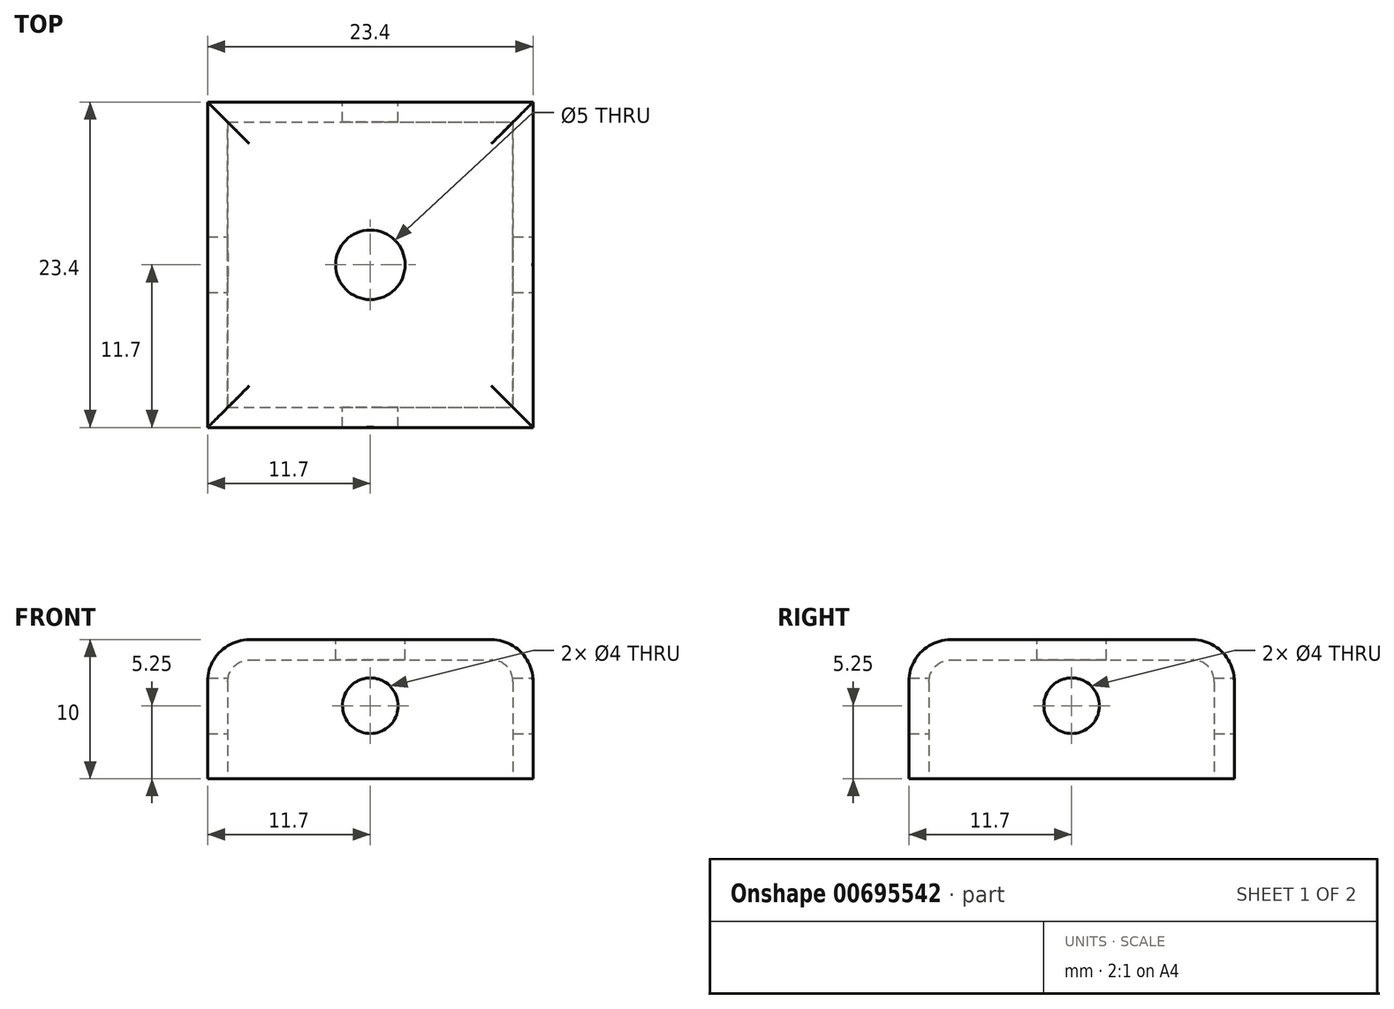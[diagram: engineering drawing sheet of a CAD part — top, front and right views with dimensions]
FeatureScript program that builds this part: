
annotation { "Feature Type Name" : "Feature", "Feature Type Description" : "" }
export const myFeature = defineFeature(function(context is Context, id is Id, definition is map)
    precondition{}
    {
        {
            var Q0;
            Q0=qCreatedBy(makeId("Top.planeOp"),FACE);
            var sketch = newSketch(context, id + "F0", { "sketchPlane" : qUnion([Q0])});
            skLineSegment(sketch, "E0.bottom", {"start": v(-11.7, 11.7) * mm, "end": v(11.7, 11.7) * mm});
            skLineSegment(sketch, "E0.top", {"start": v(-11.7, -11.7) * mm, "end": v(11.7, -11.7) * mm});
            skLineSegment(sketch, "E0.left", {"start": v(-11.7, 11.7) * mm, "end": v(-11.7, -11.7) * mm});
            skLineSegment(sketch, "E0.right", {"start": v(11.7, 11.7) * mm, "end": v(11.7, -11.7) * mm});
            skPoint(sketch, "E0.middle", {"position": v(0, 0) * mm});
            skSolve(sketch);
        }
        {
            var Q0;
            Q0=makeQuery(id+"F0.imprint","IMPRINT",FACE,{"disambiguationData":[TD([[makeQuery(id+"F0.imprint","IMPRINT",EDGE,{"derivedFrom":sQuery(id+"F0.wireOp",EDGE,"E0.bottom")}),-1.0]])]});
            extrude(context, id + "F1", {"entities" : qUnion([Q0]), "depth" : 10 * mm, "offsetDistance" : 25 * mm});
        }
        {
            var Q0;
            Q0=makeQuery(id+"F1.opExtrude","CAP_FACE",FACE,{"disambiguationData":[OSD([sQuery(id+"F0.wireOp",EDGE,"E0.bottom"),sQuery(id+"F0.wireOp",EDGE,"E0.top"),sQuery(id+"F0.wireOp",EDGE,"E0.left"),sQuery(id+"F0.wireOp",EDGE,"E0.right")])],"isStart":false});
            fillet(context, id + "F2", {"entities" : qUnion([Q0]), "radius" : 3 * mm, "tangentPropagation" : true, "allowEdgeOverflow" : false});
        }
        {
            var Q0;
            Q0=makeQuery(id+"F1.opExtrude","CAP_FACE",FACE,{"disambiguationData":[OSD([sQuery(id+"F0.wireOp",EDGE,"E0.bottom"),sQuery(id+"F0.wireOp",EDGE,"E0.top"),sQuery(id+"F0.wireOp",EDGE,"E0.left"),sQuery(id+"F0.wireOp",EDGE,"E0.right")])],"isStart":false});
            var sketch = newSketch(context, id + "F3", { "sketchPlane" : qUnion([Q0])});
            skSolve(sketch);
        }
        {
            var Q0;
            {var subQ0=sQuery(id+"F0.wireOp",EDGE,"E0.right");var subQ1=sQuery(id+"F0.wireOp",EDGE,"E0.left");var subQ2=sQuery(id+"F0.wireOp",EDGE,"E0.top");var subQ3=sQuery(id+"F0.wireOp",EDGE,"E0.bottom");var subQ4=makeQuery(id+"F1.opExtrude","CAP_FACE",FACE,{"disambiguationData":[OSD([subQ3,subQ2,subQ1,subQ0])],"isStart":false});Q0=makeQuery(id+"F3.imprint","IMPRINT",FACE,{"disambiguationData":[TD([[makeQuery(id+"F3.imprint","IMPRINT",EDGE,{"derivedFrom":makeQuery(id+"F2.opFillet","BLEND_EDGE",EDGE,{"blendedFrom":[makeQuery(id+"F1.opExtrude","CAP_EDGE",EDGE,{"disambiguationData":[OSD([subQ3])],"isStart":false}),subQ4],"blendedInto":[subQ4]})}),1.0]])]});}
            var sketch = newSketch(context, id + "F4", { "sketchPlane" : qUnion([Q0])});
            skLineSegment(sketch, "E1", {"start": v(0, 0) * mm, "end": v(0, -8.52) * mm});
            skLineSegment(sketch, "E2", {"start": v(0, -8.52) * mm, "end": v(9.06, 0) * mm});
            skLineSegment(sketch, "E3", {"start": v(9.06, 0) * mm, "end": v(0, 0) * mm});
            skSolve(sketch);
        }
        {
            var Q0;
            Q0=makeQuery(id+"F1.opExtrude","CAP_FACE",FACE,{"disambiguationData":[OSD([sQuery(id+"F0.wireOp",EDGE,"E0.bottom"),sQuery(id+"F0.wireOp",EDGE,"E0.top"),sQuery(id+"F0.wireOp",EDGE,"E0.left"),sQuery(id+"F0.wireOp",EDGE,"E0.right")])],"isStart":true});
            shell(context, id + "F5", {"entities" : qUnion([Q0]), "thickness" : 1.45 * mm});
        }
        {
            var Q0;
            Q0=makeQuery(id+"F1.opExtrude","SWEPT_FACE",FACE,{"disambiguationData":[OSD([sQuery(id+"F0.wireOp",EDGE,"E0.right")])]});
            var sketch = newSketch(context, id + "F6", { "sketchPlane" : qUnion([Q0])});
            skLineSegment(sketch, "E4", {"start": v(0, 7) * mm, "end": v(0, 0) * mm});
            skLineSegment(sketch, "E5", {"start": v(0, 0) * mm, "end": v(0, 3.5) * mm});
            skLineSegment(sketch, "E6", {"start": v(0, 3.5) * mm, "end": v(0, 7) * mm});
            skLineSegment(sketch, "E7", {"start": v(0, 5.25) * mm, "end": v(0, 3.5) * mm});
            skSolve(sketch);
        }
        {
            var Q0;
            Q0=sQuery(id+"F6.wireOp",VERTEX,"E7.start");
            var Q1;
            Q1=makeQuery(id+"F1.opExtrude","SWEPT_BODY",BODY,{"disambiguationData":[OSD([sQuery(id+"F0.wireOp",EDGE,"E0.bottom"),sQuery(id+"F0.wireOp",EDGE,"E0.top"),sQuery(id+"F0.wireOp",EDGE,"E0.left"),sQuery(id+"F0.wireOp",EDGE,"E0.right")])]});
            hole(context, id + "F7", {"style" : HoleStyle.SIMPLE, "endStyle" : HoleEndStyle.THROUGH, "holeDiameter" : 4 * mm, "majorDiameter" : 5 * mm, "isTappedThrough" : true, "tappedDepth" : 12 * mm, "tapClearance" : 3, "locations" : qUnion([Q0]), "scope" : qUnion([Q1])});
        }
        {
            var Q0;
            Q0=sQuery(id+"F4.wireOp",VERTEX,"E1.start");
            var Q1;
            Q1=makeQuery(id+"F1.opExtrude","SWEPT_BODY",BODY,{"disambiguationData":[OSD([sQuery(id+"F0.wireOp",EDGE,"E0.bottom"),sQuery(id+"F0.wireOp",EDGE,"E0.top"),sQuery(id+"F0.wireOp",EDGE,"E0.left"),sQuery(id+"F0.wireOp",EDGE,"E0.right")])]});
            hole(context, id + "F8", {"style" : HoleStyle.SIMPLE, "endStyle" : HoleEndStyle.THROUGH, "holeDiameter" : 5 * mm, "majorDiameter" : 5 * mm, "isTappedThrough" : true, "tappedDepth" : 12 * mm, "tapClearance" : 3, "locations" : qUnion([Q0]), "scope" : qUnion([Q1])});
        }
        {
            var Q0;
            Q0=makeQuery(id+"F1.opExtrude","SWEPT_FACE",FACE,{"disambiguationData":[OSD([sQuery(id+"F0.wireOp",EDGE,"E0.bottom")])]});
            var sketch = newSketch(context, id + "F9", { "sketchPlane" : qUnion([Q0])});
            skLineSegment(sketch, "E8", {"start": v(0, 0) * mm, "end": v(0, 7) * mm});
            skLineSegment(sketch, "E9", {"start": v(0, 7) * mm, "end": v(0, 3.5) * mm});
            skLineSegment(sketch, "E10", {"start": v(0, 3.5) * mm, "end": v(0, 5.25) * mm});
            skSolve(sketch);
        }
        {
            var Q0;
            Q0=sQuery(id+"F9.wireOp",VERTEX,"E10.end");
            var Q1;
            Q1=makeQuery(id+"F1.opExtrude","SWEPT_BODY",BODY,{"disambiguationData":[OSD([sQuery(id+"F0.wireOp",EDGE,"E0.bottom"),sQuery(id+"F0.wireOp",EDGE,"E0.top"),sQuery(id+"F0.wireOp",EDGE,"E0.left"),sQuery(id+"F0.wireOp",EDGE,"E0.right")])]});
            hole(context, id + "F10", {"style" : HoleStyle.SIMPLE, "endStyle" : HoleEndStyle.THROUGH, "holeDiameter" : 4 * mm, "majorDiameter" : 5 * mm, "isTappedThrough" : true, "tappedDepth" : 12 * mm, "tapClearance" : 3, "locations" : qUnion([Q0]), "scope" : qUnion([Q1])});
        }
    });
